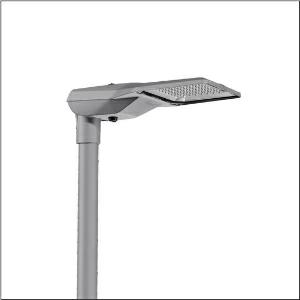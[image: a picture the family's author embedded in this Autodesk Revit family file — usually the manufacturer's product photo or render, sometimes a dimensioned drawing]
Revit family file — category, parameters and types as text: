
# Revit family: streetlight_sl_21_midi___st1_5a_5xe3p33t08lb_3dd1
name_source: partatom
category: Lighting Fixtures
units: mm (PartAtom-declared; Revit-internal decimal feet)

## family parameters
Cut with Voids When Loaded = No
Host = Face
Light Source = No
Part Type = Normal
Room Calculation Point = No
Round Connector Dimension = Use Diameter
Shared = No

## types (1)
- --- (1 x LED, 14100 lm, 98.3 W, 3000K)
    Apparent Load = 98 VA
    CIE Flux Codes = 22 53 95 100 100
    Color Rendering = 70
    Color Temperature = 3000K
    Default Elevation = 1800 mm
    Description = Streetlight SL 21 midi, mast luminaire, primary light control with lens, of PMMA, primary optical cover: cover, of toughened safety glass, transparent, light distribution: ST1.5a, light emission: direct distribution, primary light characteristic: asymmetric, installation type: side-entry, post-top, LED, High Power LED, rated luminous flux: 14.100lm, luminous efficacy: 143lm/W, light colour: 730, colour temperature: 3000K, control: overheat protection, constant luminous flux control, time-dependent luminous flux control, flexible luminous flux parameterisation, presetting dimming logarithmic, mains connection: 230..240V, AC, 50/60Hz, start of lifetime: 98W, end of service life: 101W, reduction: 45W, luminaire housing, of diecast aluminium, powder-coated, Siteco® metallic grey (DB 702S), corrosivity category C5 mid according to DIN EN ISO 12944, please order mast flange separately, inclination adjustable: 0°, 5°, 10°, 15°, sealing non-destructively replaceable, multi-level sealing system, length: 644mm, width: 335mm, height: 110mm, mast flange for spigot size: 42mm (side-entry): 5XC10008XM4, 60/48mm (side-entry/post-top): 5XC10108XM2, 76/60mm (side-entry/post-top): 5XC10108XM1, Smart Interface below and above, protection rating (complete): IP66, insulation class (complete): insulation class II (safety insulation), certification: CE, ENEC, ENEC+, VDE, impact resistance: IK09, permissible operating ambient temperature for outdoor applications: -40..+50°C, standard-compliant lighting for roads and squares, packaging unit: 1 piece

Light Distribution: ST1.5a
    Height = 111 mm
    Lamp = 1 x LED
    Lamp Light Flux = 14100 lm
    Lamp Power = 98.3 W
    Lamp count = 1
    Length = 644 mm
    Luminous efficacy = 143 lm/W
    Manufacturer = Siteco
    ModVariant = No
    Model = 5XE3P33T08LB
    Number of Poles = 1
    OnlyDefault = Yes
    Power Factor = 1
    Product Name = Streetlight SL 21 midi | ST1.5a
    Product group = mast luminaire | pylon top
    ProductGroupID = 6100
    Protection Class = Protection class II
    Protection Degree = IP 66
    RLX_Detail_Level = 1
    RLX_Emergency_Light_Flux = 0 lm
    RLX_Emergency_Type = 0
    RLX_Emergency_Type_DB = No
    RlxData = <blob elided: 95201 chars, md5=204d47b0>
    Socket = socket
    Standby Power = 0 W
    System Light Flux = 14100 lm
    System Power = 98 W
    Type Comments = factory setting: luminous flux: 100 % | dim-lin: 254 | 1020 mA
    Type Image = l_1004304.jpg
    URL = http://relux.com
    VarID = @adj_109395
    Voltage = 0 V
    Weight = 0.00 kg
    Width = 336 mm

## geometry (parser evidence)
native form markers: Blend x4, Sweep x8
no freeform markers — native parametric forms only
